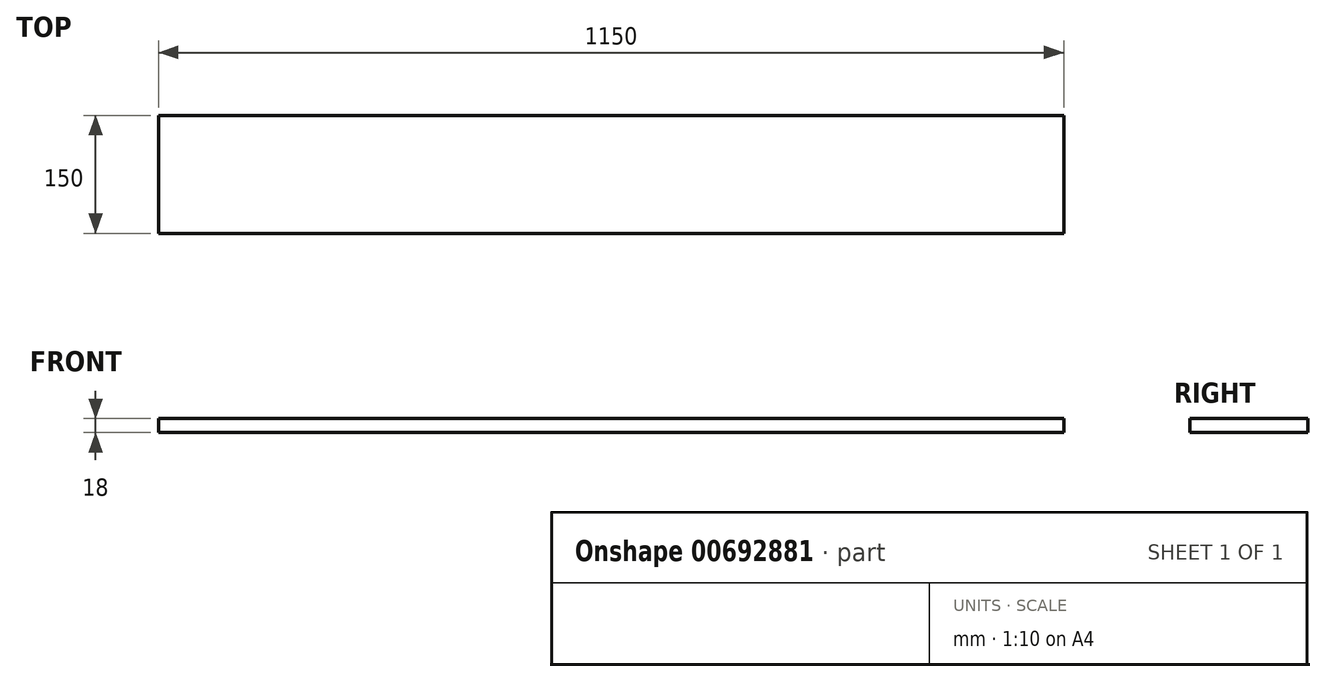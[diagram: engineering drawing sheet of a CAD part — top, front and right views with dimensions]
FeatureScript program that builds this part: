
annotation { "Feature Type Name" : "Feature", "Feature Type Description" : "" }
export const myFeature = defineFeature(function(context is Context, id is Id, definition is map)
    precondition{}
    {
        {
            var Q0;
            Q0=qCreatedBy(makeId("Top.planeOp"),FACE);
            var sketch = newSketch(context, id + "F0", { "sketchPlane" : qUnion([Q0])});
            skLineSegment(sketch, "E0.bottom", {"start": v(575, 75) * mm, "end": v(-575, 75) * mm});
            skLineSegment(sketch, "E0.top", {"start": v(575, -75) * mm, "end": v(-575, -75) * mm});
            skLineSegment(sketch, "E0.left", {"start": v(575, 75) * mm, "end": v(575, -75) * mm});
            skLineSegment(sketch, "E0.right", {"start": v(-575, 75) * mm, "end": v(-575, -75) * mm});
            skPoint(sketch, "E0.middle", {"position": v(0, 0) * mm});
            skSolve(sketch);
        }
        {
            var Q0;
            Q0 = qSketchRegion(id + "F0", true);
            extrude(context, id + "F1", {"entities" : qUnion([Q0]), "depth" : 18 * mm, "offsetDistance" : 25 * mm});
        }
    });
